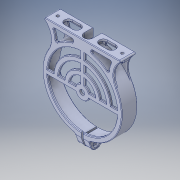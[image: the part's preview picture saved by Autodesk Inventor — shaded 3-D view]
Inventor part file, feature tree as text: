
AUTODESK INVENTOR PART (.ipt)
format: ipt  version: 2016 (Build 200138000, 138)  size: 700,416 bytes
history: native  units: in
note: dims shown in document units (in); Inventor stores cm internally (conversion verified against a paired STEP export)
features: mirror x1
ambient origin geometry x8: Origin, YZ Plane, XZ Plane, XY Plane, X Axis, Y Axis, Z Axis, Center Point
bodies: Solid1 (feature_tree)
feature tree (1):
  mirror  "Mirror3"
